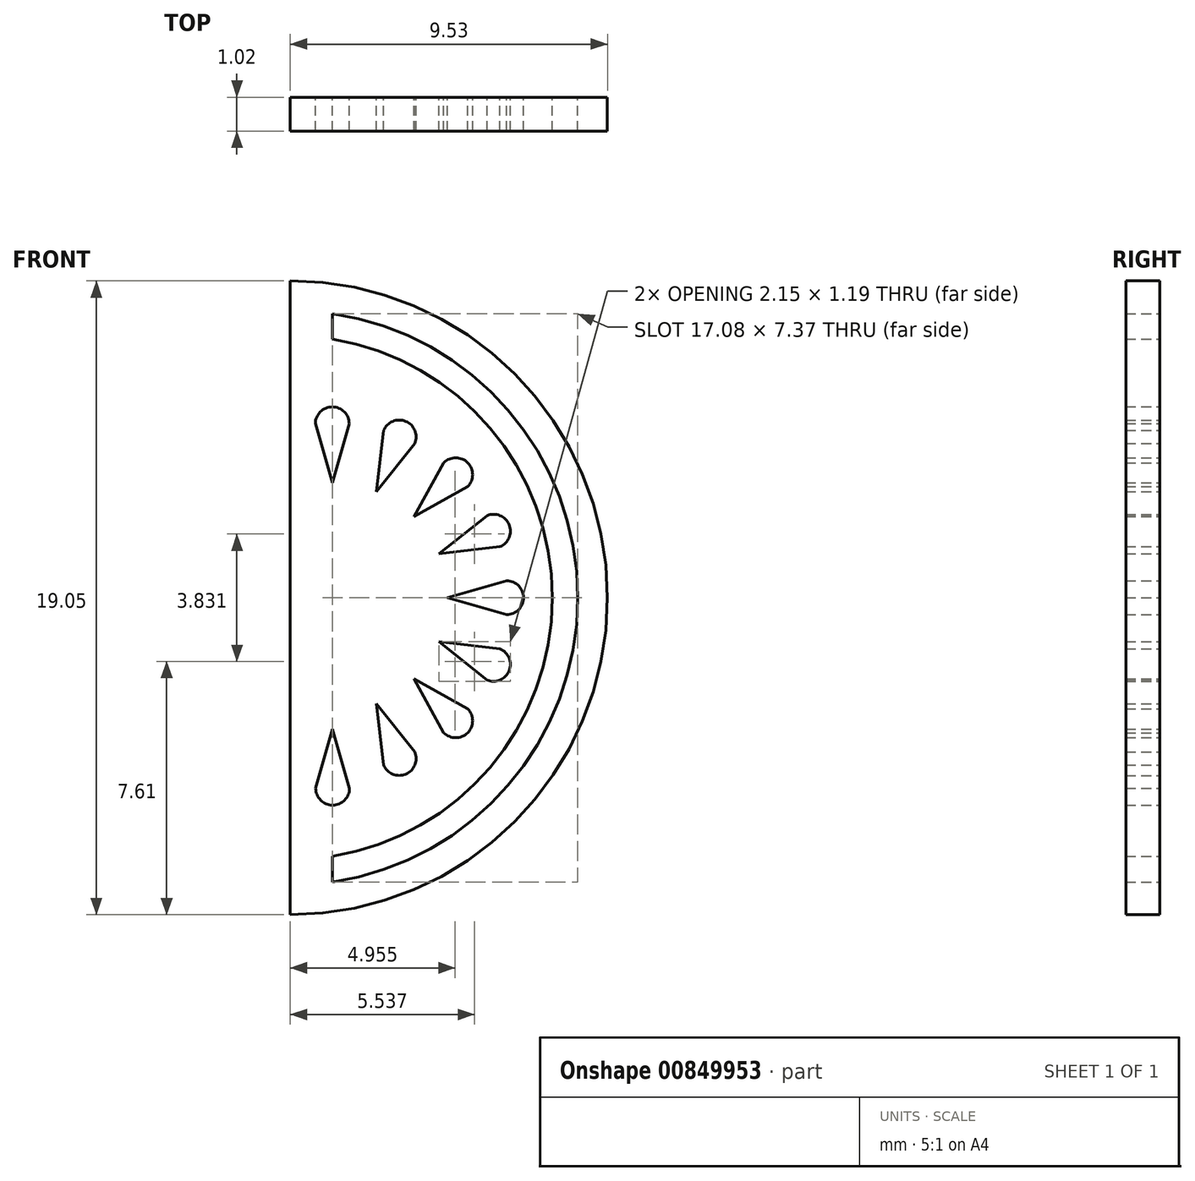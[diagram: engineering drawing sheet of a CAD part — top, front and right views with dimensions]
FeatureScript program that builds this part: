
annotation { "Feature Type Name" : "Feature", "Feature Type Description" : "" }
export const myFeature = defineFeature(function(context is Context, id is Id, definition is map)
    precondition{}
    {
        {
            var Q0;
            Q0=qCreatedBy(makeId("Front.planeOp"),FACE);
            var sketch = newSketch(context, id + "F0", { "sketchPlane" : qUnion([Q0])});
            skArc(sketch, "E0", {"start": v(0.87, -10.06) * mm, "mid": v(10.4, -0.53) * mm, "end": v(0.87, 9) * mm});
            skLineSegment(sketch, "E1", {"start": v(0.87, -10.06) * mm, "end": v(0.87, 9) * mm});
            skArc(sketch, "E2.1", {"start": v(2.14, -9.08) * mm, "mid": v(9.5, -0.53) * mm, "end": v(2.14, 8) * mm});
            skArc(sketch, "E3.0", {"start": v(2.14, -8.3) * mm, "mid": v(8.75, -0.53) * mm, "end": v(2.14, 7.24) * mm});
            skLineSegment(sketch, "E4", {"start": v(2.14, 8) * mm, "end": v(2.14, -9.08) * mm, "construction": true});
            skLineSegment(sketch, "E5", {"start": v(2.14, 8) * mm, "end": v(2.14, 7.24) * mm});
            skLineSegment(sketch, "E6", {"start": v(2.14, -8.3) * mm, "end": v(2.14, -9.08) * mm});
            skLineSegment(sketch, "E7", {"start": v(2.14, 4.7) * mm, "end": v(2.14, 3.53) * mm, "construction": true});
            skPoint(sketch, "E8", {"position": v(2.14, -0.53) * mm});
            skLineSegment(sketch, "E9.1.0", {"start": v(3.67, 4.5) * mm, "end": v(3.46, 2.66) * mm});
            skArc(sketch, "E9.1.1", {"start": v(4.61, 4.1) * mm, "mid": v(4.34, 4.77) * mm, "end": v(3.67, 4.5) * mm});
            skLineSegment(sketch, "E9.1.2", {"start": v(3.46, 2.66) * mm, "end": v(4.61, 4.1) * mm});
            skLineSegment(sketch, "E9.2.0", {"start": v(5.48, 3.52) * mm, "end": v(4.58, 1.9) * mm});
            skArc(sketch, "E9.2.1", {"start": v(6.2, 2.8) * mm, "mid": v(6.2, 3.52) * mm, "end": v(5.48, 3.52) * mm});
            skLineSegment(sketch, "E9.2.2", {"start": v(4.58, 1.9) * mm, "end": v(6.2, 2.8) * mm});
            skLineSegment(sketch, "E9.3.0", {"start": v(6.78, 1.94) * mm, "end": v(5.33, 0.79) * mm});
            skArc(sketch, "E9.3.1", {"start": v(7.17, 1) * mm, "mid": v(7.44, 1.66) * mm, "end": v(6.78, 1.94) * mm});
            skLineSegment(sketch, "E9.3.2", {"start": v(5.33, 0.79) * mm, "end": v(7.17, 1) * mm});
            skLineSegment(sketch, "E9.4.0", {"start": v(7.37, -0.03) * mm, "end": v(5.6, -0.53) * mm});
            skArc(sketch, "E9.4.1", {"start": v(7.37, -1.04) * mm, "mid": v(7.88, -0.53) * mm, "end": v(7.37, -0.03) * mm});
            skLineSegment(sketch, "E9.4.2", {"start": v(5.6, -0.53) * mm, "end": v(7.37, -1.04) * mm});
            skLineSegment(sketch, "E9.5.0", {"start": v(7.17, -2.07) * mm, "end": v(5.33, -1.86) * mm});
            skArc(sketch, "E9.5.1", {"start": v(6.78, -3) * mm, "mid": v(7.44, -2.73) * mm, "end": v(7.17, -2.07) * mm});
            skLineSegment(sketch, "E9.5.2", {"start": v(5.33, -1.86) * mm, "end": v(6.78, -3) * mm});
            skLineSegment(sketch, "E9.6.0", {"start": v(6.2, -3.87) * mm, "end": v(4.58, -2.98) * mm});
            skArc(sketch, "E9.6.1", {"start": v(5.48, -4.6) * mm, "mid": v(6.2, -4.6) * mm, "end": v(6.2, -3.87) * mm});
            skLineSegment(sketch, "E9.6.2", {"start": v(4.58, -2.98) * mm, "end": v(5.48, -4.6) * mm});
            skLineSegment(sketch, "E9.7.0", {"start": v(4.61, -5.17) * mm, "end": v(3.46, -3.73) * mm});
            skArc(sketch, "E9.7.1", {"start": v(3.67, -5.56) * mm, "mid": v(4.34, -5.84) * mm, "end": v(4.61, -5.17) * mm});
            skLineSegment(sketch, "E9.7.2", {"start": v(3.46, -3.73) * mm, "end": v(3.67, -5.56) * mm});
            skLineSegment(sketch, "E9.anchor1", {"start": v(2.14, -0.53) * mm, "end": v(2.14, 2.92) * mm, "construction": true});
            skLineSegment(sketch, "E10.1.0", {"start": v(1.62, 4.7) * mm, "end": v(2.14, 2.92) * mm});
            skArc(sketch, "E10.1.1", {"start": v(2.64, 4.7) * mm, "mid": v(2.13, 5.2) * mm, "end": v(1.62, 4.7) * mm});
            skLineSegment(sketch, "E10.1.2", {"start": v(2.14, 2.92) * mm, "end": v(2.64, 4.7) * mm});
            skLineSegment(sketch, "E11", {"start": v(1.62, 4.7) * mm, "end": v(2.64, 4.7) * mm, "construction": true});
            skLineSegment(sketch, "E12", {"start": v(2.13, 4.7) * mm, "end": v(2.14, 2.92) * mm, "construction": true});
            skLineSegment(sketch, "E13.1.0", {"start": v(2.65, -6.26) * mm, "end": v(2.14, -4.48) * mm});
            skArc(sketch, "E13.1.1", {"start": v(1.63, -6.26) * mm, "mid": v(2.14, -6.77) * mm, "end": v(2.65, -6.26) * mm});
            skLineSegment(sketch, "E13.1.2", {"start": v(2.14, -4.48) * mm, "end": v(1.63, -6.26) * mm});
            skLineSegment(sketch, "E14", {"start": v(1.63, -6.26) * mm, "end": v(2.65, -6.26) * mm, "construction": true});
            skLineSegment(sketch, "E15", {"start": v(2.14, -4.48) * mm, "end": v(2.14, -6.26) * mm, "construction": true});
            skFitSpline(sketch, "E16", {"points": [v(0.94, 9.04) * mm, v(0.04, 8.84) * mm, v(-0.52, 11.37) * mm, v(1.45, 9.73) * mm, v(0.94, 9.04) * mm]});
            skLineSegment(sketch, "E17", {"start": v(0.04, 8.84) * mm, "end": v(1.45, 9.73) * mm, "construction": true});
            skFitSpline(sketch, "E18.0", {"points": [v(1.48, 8.33) * mm, v(1.41, 8.3) * mm, v(1.35, 8.25) * mm, v(1.25, 8.18) * mm, v(1.1, 8.08) * mm, v(0.83, 7.94) * mm, v(0.5, 7.84) * mm, v(0.18, 7.84) * mm, v(-0.08, 7.9) * mm, v(-0.33, 8) * mm, v(-0.53, 8.14) * mm, v(-0.7, 8.3) * mm, v(-0.87, 8.52) * mm, v(-1.04, 8.8) * mm, v(-1.2, 9.15) * mm, v(-1.35, 9.53) * mm, v(-1.46, 9.91) * mm, v(-1.54, 10.3) * mm, v(-1.58, 10.64) * mm, v(-1.59, 10.9) * mm, v(-1.57, 11.1) * mm, v(-1.54, 11.32) * mm, v(-1.47, 11.56) * mm, v(-1.34, 11.82) * mm, v(-1.13, 12.04) * mm, v(-0.9, 12.18) * mm, v(-0.68, 12.27) * mm, v(-0.4, 12.3) * mm, v(-0.14, 12.28) * mm, v(0.09, 12.22) * mm, v(0.28, 12.14) * mm, v(0.52, 12.02) * mm, v(0.8, 11.84) * mm, v(1.1, 11.6) * mm, v(1.4, 11.32) * mm, v(1.68, 11.03) * mm, v(1.92, 10.73) * mm, v(2.1, 10.46) * mm, v(2.22, 10.23) * mm, v(2.32, 9.97) * mm, v(2.38, 9.64) * mm, v(2.33, 9.3) * mm, v(2.24, 9.05) * mm, v(2.12, 8.86) * mm, v(1.95, 8.66) * mm, v(1.74, 8.5) * mm, v(1.58, 8.4) * mm, v(1.48, 8.33) * mm, v(1.41, 8.3) * mm, v(1.35, 8.25) * mm, v(1.48, 8.33) * mm]});
            skSolve(sketch);
        }
        {
            var Q0;
            {var subQ8=sQuery(id+"F0.wireOp",EDGE,"85690892-09ce-4fc8-9afb-38caa5ee72fe.0");Q0=makeQuery(id+"F0.imprint","IMPRINT",FACE,{"disambiguationData":[TD([[makeQuery(id+"F0.imprint","IMPRINT",EDGE,{"derivedFrom":subQ8}),-1.0]])]});}
            var Q1;
            {var subQ1=sQuery(id+"F0.wireOp",EDGE,"E0");var subQ3=sQuery(id+"F0.wireOp",EDGE,"85690892-09ce-4fc8-9afb-38caa5ee72fe.6");var subQ4=makeQuery(id+"F0.imprint","INTERSECT",VERTEX,{"derivedFrom":[subQ1,subQ3]});Q1=makeQuery(id+"F0.imprint","IMPRINT",FACE,{"disambiguationData":[TD([[makeQuery(id+"F0.imprint","IMPRINT",EDGE,{"disambiguationData":[TD([[subQ4,-1.0]])],"derivedFrom":subQ3}),-1.0]])]});}
            var Q2;
            Q2=makeQuery(id+"F0.imprint","IMPRINT",FACE,{"disambiguationData":[TD([[makeQuery(id+"F0.imprint","IMPRINT",EDGE,{"derivedFrom":sQuery(id+"F0.wireOp",EDGE,"E2.1")}),-1.0]])]});
            var Q3;
            Q3=makeQuery(id+"F0.imprint","IMPRINT",FACE,{"disambiguationData":[TD([[makeQuery(id+"F0.imprint","IMPRINT",EDGE,{"derivedFrom":sQuery(id+"F0.wireOp",EDGE,"uL7xLaIb-4X59-XXva-hb91-jbXrVA5aCHRa")}),-1.0]])]});
            var Q4;
            {var subQ0=sQuery(id+"F0.wireOp",EDGE,"E1");var subQ1=sQuery(id+"F0.wireOp",EDGE,"E0");var subQ2=makeQuery(id+"F0.imprint","INTERSECT",VERTEX,{"disambiguationData":[OD(1.0)],"derivedFrom":[subQ1,subQ0]});Q4=makeQuery(id+"F0.imprint","IMPRINT",FACE,{"disambiguationData":[TD([[makeQuery(id+"F0.imprint","IMPRINT",EDGE,{"disambiguationData":[TD([[subQ2,1.0]])],"derivedFrom":subQ1}),1.0]])]});}
            var Q5;
            Q5=makeQuery(id+"F0.imprint","IMPRINT",FACE,{"disambiguationData":[TD([[makeQuery(id+"F0.imprint","IMPRINT",EDGE,{"derivedFrom":sQuery(id+"F0.wireOp",EDGE,"E16")}),1.0]])]});
            extrude(context, id + "F1", {"entities" : qUnion([Q0, Q1, Q2, Q3, Q4, Q5]), "depth" : 1.02 * mm, "offsetDistance" : 25.4 * mm});
        }
    });
